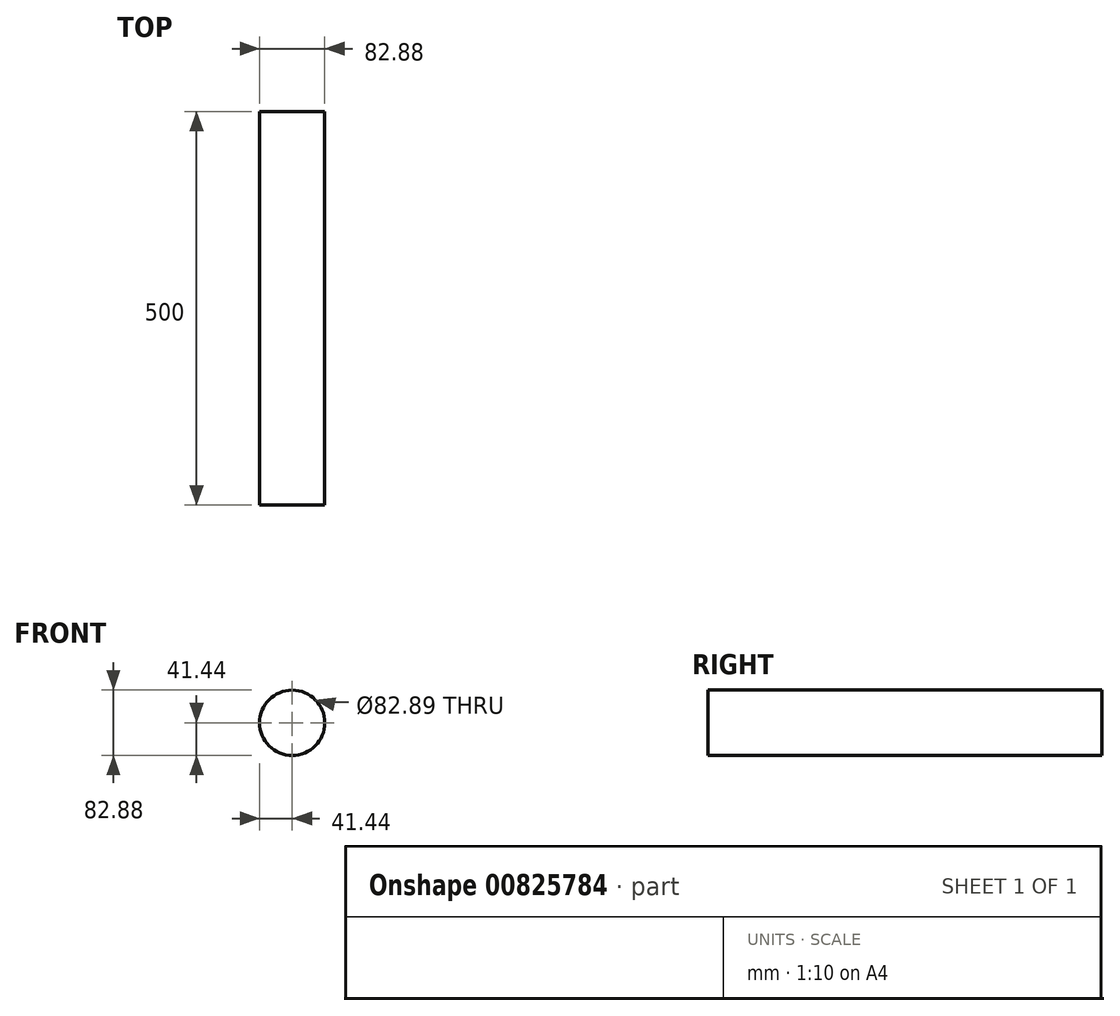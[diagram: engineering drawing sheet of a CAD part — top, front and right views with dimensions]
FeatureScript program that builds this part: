
annotation { "Feature Type Name" : "Feature", "Feature Type Description" : "" }
export const myFeature = defineFeature(function(context is Context, id is Id, definition is map)
    precondition{}
    {
        {
            var Q0;
            Q0=qCreatedBy(makeId("Front.planeOp"),FACE);
            var sketch = newSketch(context, id + "F0", { "sketchPlane" : qUnion([Q0])});
            skCircle(sketch, "E0", {"center": v(0, 0) * mm, "radius": 41.44 * mm});
            skSolve(sketch);
        }
        {
            var Q0;
            Q0=sQuery(id+"F0.wireOp",EDGE,"E0");
            extrude(context, id + "F1", {"bodyType" : ToolBodyType.SURFACE, "surfaceEntities" : qUnion([Q0]), "oppositeDirection" : true, "depth" : 1500 * mm, "offsetDistance" : 25 * mm, "hasSecondDirection" : true, "secondDirectionOppositeDirection" : true, "secondDirectionDepth" : 1000 * mm});
        }
    });
